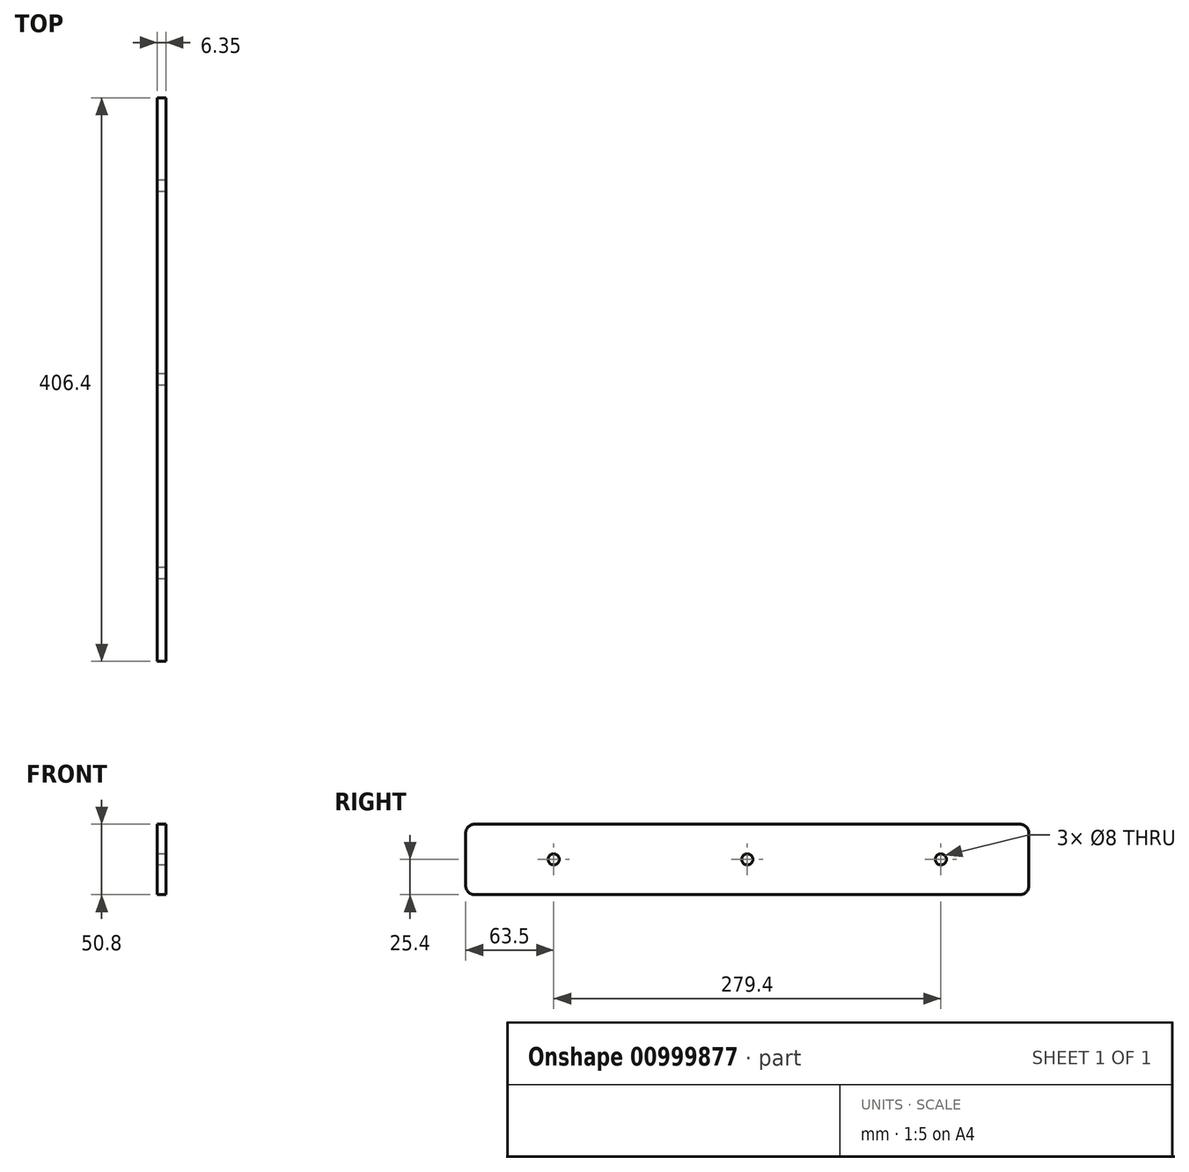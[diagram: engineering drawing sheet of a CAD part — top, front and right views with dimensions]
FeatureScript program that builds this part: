
annotation { "Feature Type Name" : "Feature", "Feature Type Description" : "" }
export const myFeature = defineFeature(function(context is Context, id is Id, definition is map)
    precondition{}
    {
        {
            var Q0;
            Q0=qCreatedBy(makeId("Right.planeOp"),FACE);
            var sketch = newSketch(context, id + "F0", { "sketchPlane" : qUnion([Q0])});
            skLineSegment(sketch, "E0.bottom", {"start": v(196.85, 25.4) * mm, "end": v(-196.85, 25.4) * mm});
            skLineSegment(sketch, "E0.top", {"start": v(196.85, -25.4) * mm, "end": v(-196.85, -25.4) * mm});
            skLineSegment(sketch, "E0.left", {"start": v(203.2, 19.05) * mm, "end": v(203.2, -19.05) * mm});
            skLineSegment(sketch, "E0.right", {"start": v(-203.2, 19.05) * mm, "end": v(-203.2, -19.05) * mm});
            skPoint(sketch, "E0.middle", {"position": v(0, 0) * mm});
            skPoint(sketch, "E1.visualSharp", {"position": v(-203.2, 25.4) * mm});
            skArc(sketch, "E1.filletArc", {"start": v(-196.85, 25.4) * mm, "mid": v(-201.34, 23.54) * mm, "end": v(-203.2, 19.05) * mm});
            skPoint(sketch, "E2.visualSharp", {"position": v(-203.2, -25.4) * mm});
            skArc(sketch, "E2.filletArc", {"start": v(-203.2, -19.05) * mm, "mid": v(-201.34, -23.54) * mm, "end": v(-196.85, -25.4) * mm});
            skPoint(sketch, "E3.visualSharp", {"position": v(203.2, 25.4) * mm});
            skArc(sketch, "E3.filletArc", {"start": v(203.2, 19.05) * mm, "mid": v(201.34, 23.54) * mm, "end": v(196.85, 25.4) * mm});
            skPoint(sketch, "E4.visualSharp", {"position": v(203.2, -25.4) * mm});
            skArc(sketch, "E4.filletArc", {"start": v(196.85, -25.4) * mm, "mid": v(201.34, -23.54) * mm, "end": v(203.2, -19.05) * mm});
            skCircle(sketch, "E5", {"center": v(0, 0) * mm, "radius": 4 * mm});
            skCircle(sketch, "E6", {"center": v(-139.7, 0) * mm, "radius": 4 * mm});
            skCircle(sketch, "E7", {"center": v(139.7, 0) * mm, "radius": 4 * mm});
            skSolve(sketch);
        }
        {
            var Q0;
            Q0=makeQuery(id+"F0.imprint","IMPRINT",FACE,{"disambiguationData":[TD([[makeQuery(id+"F0.imprint","IMPRINT",EDGE,{"derivedFrom":sQuery(id+"F0.wireOp",EDGE,"E0.bottom")}),1.0]])]});
            extrude(context, id + "F1", {"entities" : qUnion([Q0]), "depth" : 6.35 * mm, "offsetDistance" : 25.4 * mm});
        }
    });
